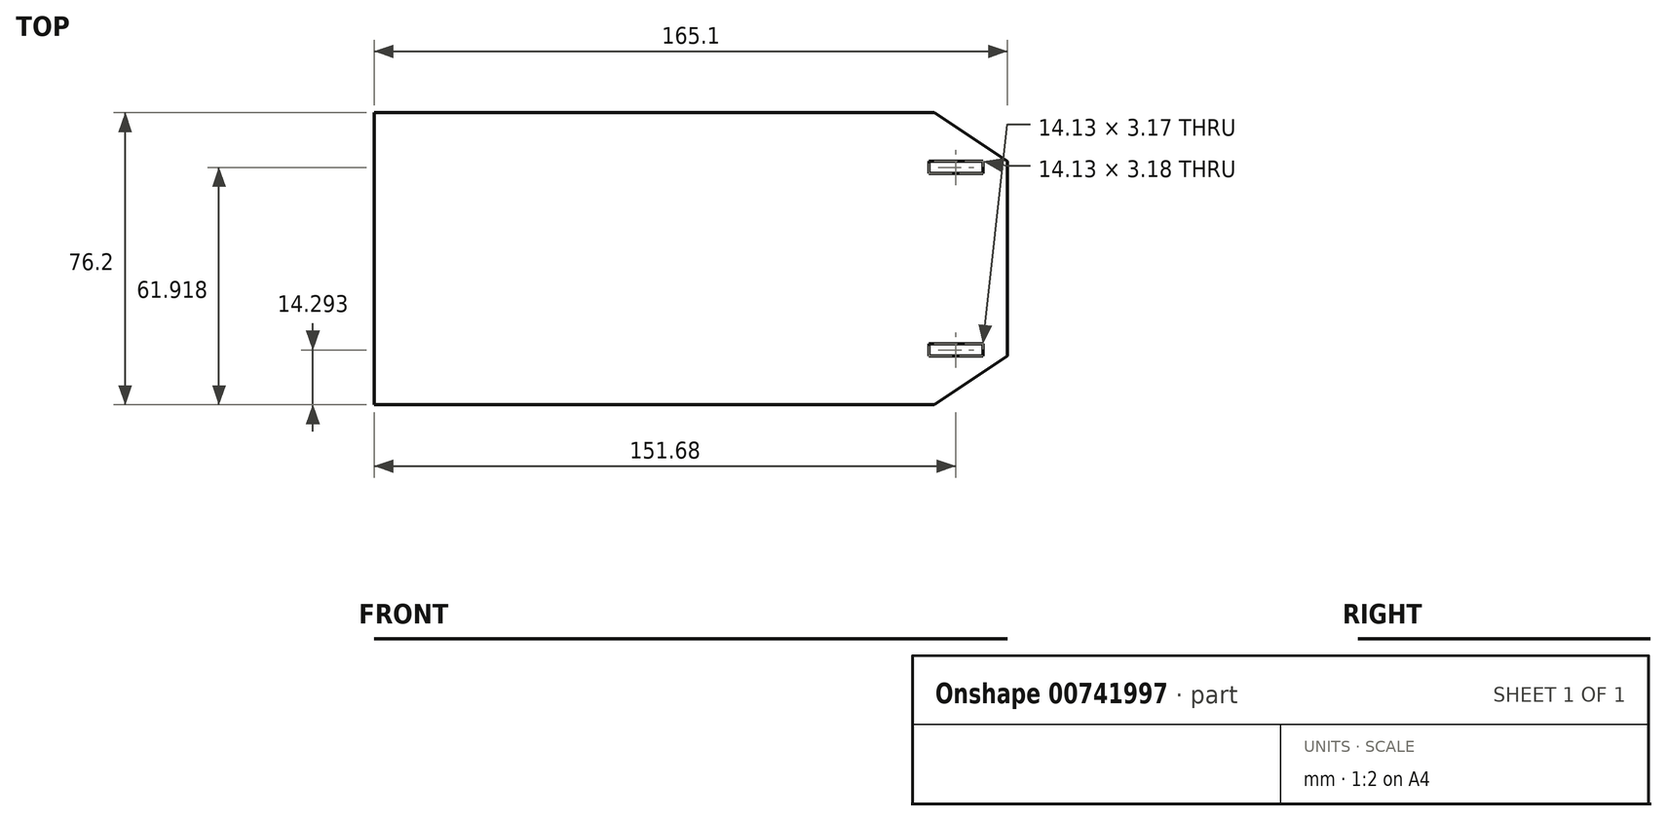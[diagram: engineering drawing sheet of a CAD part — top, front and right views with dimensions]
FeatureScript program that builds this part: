
annotation { "Feature Type Name" : "Feature", "Feature Type Description" : "" }
export const myFeature = defineFeature(function(context is Context, id is Id, definition is map)
    precondition{}
    {
        {
            var Q0;
            Q0=qCreatedBy(makeId("Top.planeOp"),FACE);
            var sketch = newSketch(context, id + "F0", { "sketchPlane" : qUnion([Q0])});
            skLineSegment(sketch, "E0.bottom", {"start": v(-61.85, 47.92) * mm, "end": v(65.15, 47.92) * mm});
            skLineSegment(sketch, "E0.top", {"start": v(-61.85, -28.28) * mm, "end": v(65.15, -28.28) * mm});
            skLineSegment(sketch, "E0.left", {"start": v(-61.85, 47.92) * mm, "end": v(-61.85, -28.28) * mm});
            skLineSegment(sketch, "E0.right", {"start": v(65.15, 47.92) * mm, "end": v(65.15, -28.28) * mm});
            skLineSegment(sketch, "E1.bottom", {"start": v(65.15, -28.28) * mm, "end": v(103.25, -28.28) * mm});
            skLineSegment(sketch, "E1.top", {"start": v(65.15, 47.92) * mm, "end": v(103.25, 47.92) * mm});
            skLineSegment(sketch, "E1.left", {"start": v(65.15, -28.28) * mm, "end": v(65.15, 47.92) * mm});
            skLineSegment(sketch, "E1.right", {"start": v(103.25, -28.28) * mm, "end": v(103.25, 47.92) * mm});
            skLineSegment(sketch, "E2", {"start": v(103.25, 47.92) * mm, "end": v(103.25, 35.22) * mm});
            skLineSegment(sketch, "E3", {"start": v(103.25, 35.22) * mm, "end": v(103.25, 47.92) * mm});
            skLineSegment(sketch, "E4", {"start": v(84.2, -28.28) * mm, "end": v(103.25, -15.58) * mm});
            skLineSegment(sketch, "E5", {"start": v(84.2, 47.92) * mm, "end": v(103.25, 35.22) * mm});
            skSolve(sketch);
        }
        {
            var Q0;
            {var subQ1=sQuery(id+"F0.wireOp",EDGE,"E0.right");Q0=makeQuery(id+"F0.imprint","IMPRINT",FACE,{"disambiguationData":[TD([[makeQuery(id+"F0.imprint","IMPRINT",EDGE,{"derivedFrom":subQ1}),1.0]])]});}
            var Q1;
            Q1=makeQuery(id+"F0.imprint","IMPRINT",FACE,{"disambiguationData":[TD([[makeQuery(id+"F0.imprint","IMPRINT",EDGE,{"derivedFrom":sQuery(id+"F0.wireOp",EDGE,"E0.bottom")}),-1.0]])]});
            extrude(context, id + "F1", {"entities" : qUnion([Q0, Q1]), "depth" : 1 / 203.2 * mm, "offsetDistance" : 25.4 * mm});
        }
        {
            var Q0;
            Q0=makeQuery(id+"F1.opExtrude","CAP_FACE",FACE,{"disambiguationData":[OSD([sQuery(id+"F0.wireOp",EDGE,"E0.bottom"),sQuery(id+"F0.wireOp",EDGE,"E0.top"),sQuery(id+"F0.wireOp",EDGE,"E0.left"),sQuery(id+"F0.wireOp",EDGE,"E1.bottom"),sQuery(id+"F0.wireOp",EDGE,"E1.top"),sQuery(id+"F0.wireOp",EDGE,"E1.right"),sQuery(id+"F0.wireOp",EDGE,"E4"),sQuery(id+"F0.wireOp",EDGE,"E5")])],"isStart":false});
            var sketch = newSketch(context, id + "F2", { "sketchPlane" : qUnion([Q0])});
            skLineSegment(sketch, "E6.bottom", {"start": v(96.9, 35.22) * mm, "end": v(82.76, 35.22) * mm});
            skLineSegment(sketch, "E6.top", {"start": v(96.9, 32.05) * mm, "end": v(82.76, 32.05) * mm});
            skLineSegment(sketch, "E6.left", {"start": v(96.9, 35.22) * mm, "end": v(96.9, 32.05) * mm});
            skLineSegment(sketch, "E6.right", {"start": v(82.76, 35.22) * mm, "end": v(82.76, 32.05) * mm});
            skLineSegment(sketch, "E7.bottom", {"start": v(96.9, -15.58) * mm, "end": v(82.76, -15.58) * mm});
            skLineSegment(sketch, "E7.top", {"start": v(96.9, -12.4) * mm, "end": v(82.76, -12.4) * mm});
            skLineSegment(sketch, "E7.left", {"start": v(96.9, -15.58) * mm, "end": v(96.9, -12.4) * mm});
            skLineSegment(sketch, "E7.right", {"start": v(82.76, -15.58) * mm, "end": v(82.76, -12.4) * mm});
            skSolve(sketch);
        }
        {
            var Q0;
            Q0=makeQuery(id+"F2.imprint","IMPRINT",FACE,{"disambiguationData":[TD([[makeQuery(id+"F2.imprint","IMPRINT",EDGE,{"derivedFrom":sQuery(id+"F2.wireOp",EDGE,"E6.bottom")}),1.0]])]});
            var Q1;
            Q1=makeQuery(id+"F2.imprint","IMPRINT",FACE,{"disambiguationData":[TD([[makeQuery(id+"F2.imprint","IMPRINT",EDGE,{"derivedFrom":sQuery(id+"F2.wireOp",EDGE,"E7.bottom")}),-1.0]])]});
            extrude(context, id + "F3", {"entities" : qUnion([Q0, Q1]), "operationType" : NewBodyOperationType.REMOVE, "oppositeDirection" : true, "depth" : 25.4 * mm, "offsetDistance" : 25.4 * mm});
        }
    });
